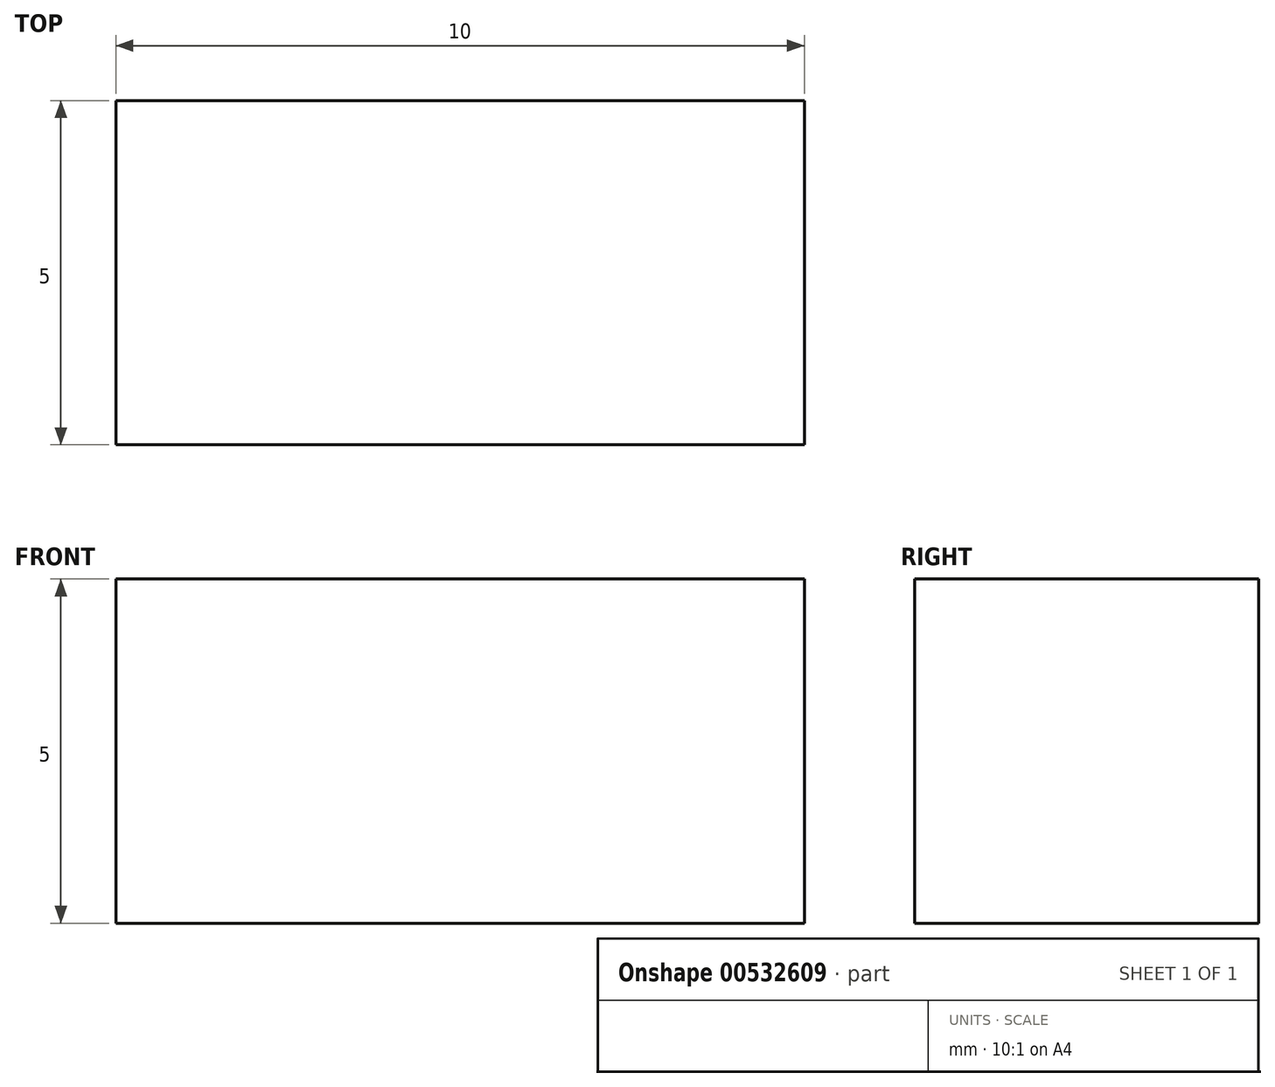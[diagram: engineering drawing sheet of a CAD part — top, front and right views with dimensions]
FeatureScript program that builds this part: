
annotation { "Feature Type Name" : "Feature", "Feature Type Description" : "" }
export const myFeature = defineFeature(function(context is Context, id is Id, definition is map)
    precondition{}
    {
        {
            var Q0;
            Q0=qCreatedBy(makeId("Top.planeOp"),FACE);
            var sketch = newSketch(context, id + "F0", { "sketchPlane" : qUnion([Q0])});
            skLineSegment(sketch, "E0.bottom", {"start": v(-5, 2.5) * mm, "end": v(5, 2.5) * mm});
            skLineSegment(sketch, "E0.top", {"start": v(-5, -2.5) * mm, "end": v(5, -2.5) * mm});
            skLineSegment(sketch, "E0.left", {"start": v(-5, 2.5) * mm, "end": v(-5, -2.5) * mm});
            skLineSegment(sketch, "E0.right", {"start": v(5, 2.5) * mm, "end": v(5, -2.5) * mm});
            skSolve(sketch);
        }
        {
            var Q0;
            Q0=makeQuery(id+"F0.imprint","IMPRINT",FACE,{"disambiguationData":[TD([[makeQuery(id+"F0.imprint","IMPRINT",EDGE,{"derivedFrom":sQuery(id+"F0.wireOp",EDGE,"E0.bottom")}),-1.0]])]});
            extrude(context, id + "F1", {"entities" : qUnion([Q0]), "depth" : 5 * mm, "offsetDistance" : 25 * mm});
        }
    });
